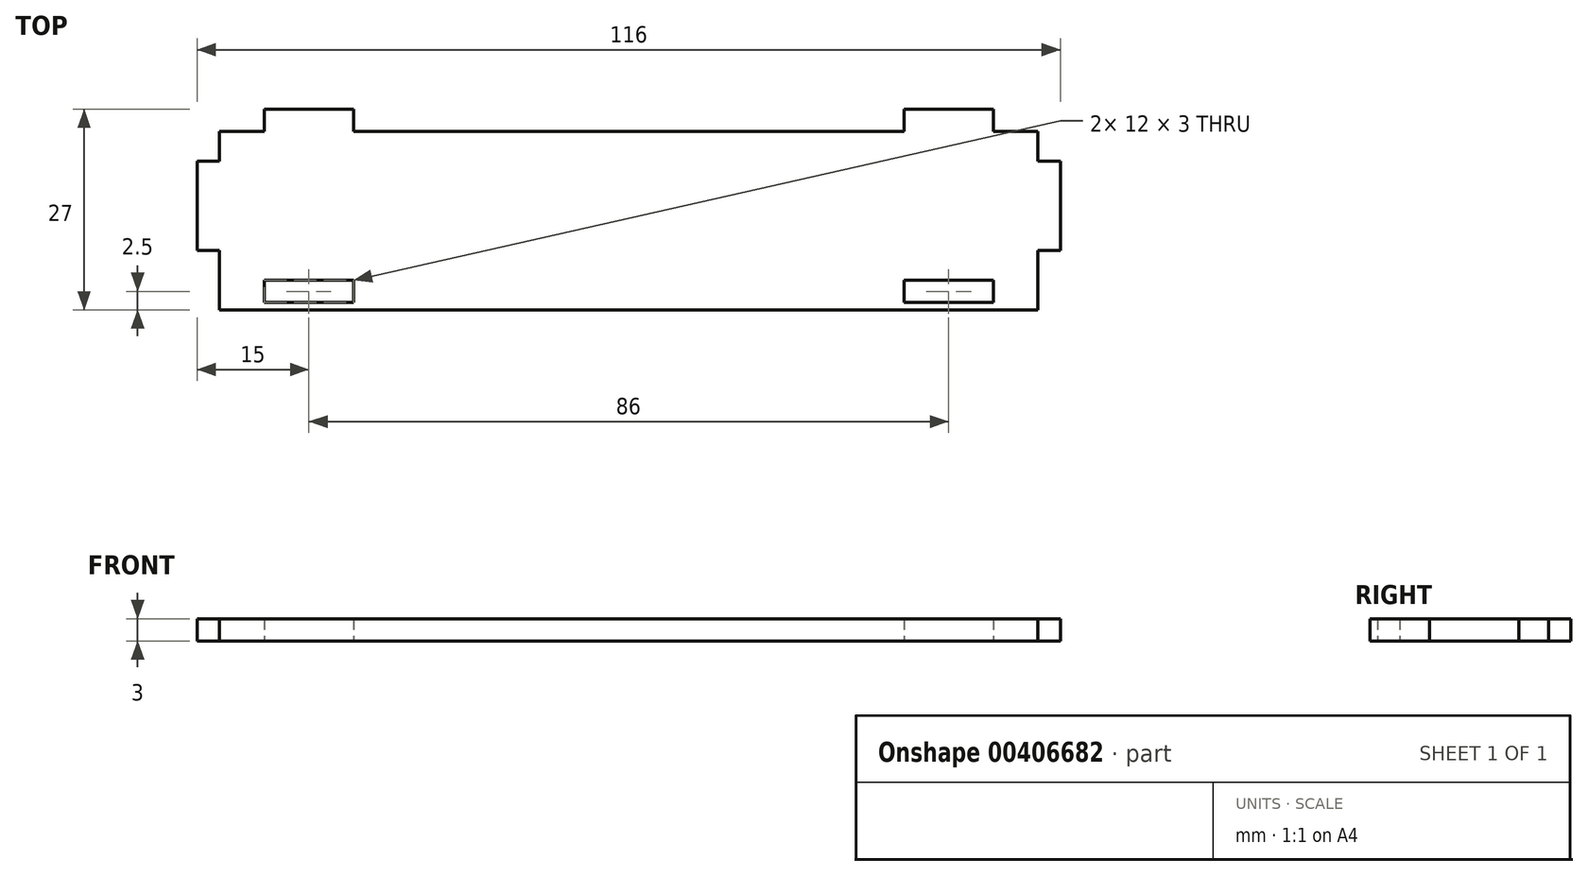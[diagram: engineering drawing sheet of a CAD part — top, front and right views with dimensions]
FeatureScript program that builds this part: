
annotation { "Feature Type Name" : "Feature", "Feature Type Description" : "" }
export const myFeature = defineFeature(function(context is Context, id is Id, definition is map)
    precondition{}
    {
        {
            var Q0;
            Q0=qCreatedBy(makeId("Top.planeOp"),FACE);
            var sketch = newSketch(context, id + "F0", { "sketchPlane" : qUnion([Q0])});
            skLineSegment(sketch, "E0.bottom", {"start": v(55, 12) * mm, "end": v(49, 12) * mm});
            skLineSegment(sketch, "E0.top", {"start": v(55, -12) * mm, "end": v(-55, -12) * mm});
            skLineSegment(sketch, "E0.left", {"start": v(55, 12) * mm, "end": v(55, 8) * mm});
            skLineSegment(sketch, "E0.right", {"start": v(-55, 12) * mm, "end": v(-55, 8) * mm});
            skPoint(sketch, "E0.middle", {"position": v(0, 0) * mm});
            skLineSegment(sketch, "E1.top", {"start": v(-49, 15) * mm, "end": v(-37, 15) * mm});
            skLineSegment(sketch, "E1.left", {"start": v(-49, 12) * mm, "end": v(-49, 15) * mm});
            skLineSegment(sketch, "E1.right", {"start": v(-37, 12) * mm, "end": v(-37, 15) * mm});
            skLineSegment(sketch, "E2.bottom", {"start": v(-49, -8) * mm, "end": v(-37, -8) * mm});
            skLineSegment(sketch, "E2.top", {"start": v(-49, -11) * mm, "end": v(-37, -11) * mm});
            skLineSegment(sketch, "E2.left", {"start": v(-49, -8) * mm, "end": v(-49, -11) * mm});
            skLineSegment(sketch, "E2.right", {"start": v(-37, -8) * mm, "end": v(-37, -11) * mm});
            skLineSegment(sketch, "E3.bottom", {"start": v(-55, 8) * mm, "end": v(-58, 8) * mm});
            skLineSegment(sketch, "E3.top", {"start": v(-55, -4) * mm, "end": v(-58, -4) * mm});
            skLineSegment(sketch, "E3.right", {"start": v(-58, 8) * mm, "end": v(-58, -4) * mm});
            skLineSegment(sketch, "E4", {"start": v(0, 0) * mm, "end": v(0, 12) * mm, "construction": true});
            skLineSegment(sketch, "E5.MirrorCS", {"start": v(37, 12) * mm, "end": v(37, 15) * mm});
            skLineSegment(sketch, "E6.MirrorCS", {"start": v(49, 15) * mm, "end": v(37, 15) * mm});
            skLineSegment(sketch, "E7.MirrorCS", {"start": v(49, 12) * mm, "end": v(49, 15) * mm});
            skLineSegment(sketch, "E8.MirrorCS", {"start": v(55, 8) * mm, "end": v(58, 8) * mm});
            skLineSegment(sketch, "E9.MirrorCS", {"start": v(58, 8) * mm, "end": v(58, -4) * mm});
            skLineSegment(sketch, "E10.MirrorCS", {"start": v(55, -4) * mm, "end": v(58, -4) * mm});
            skLineSegment(sketch, "E11.MirrorCS", {"start": v(49, -8) * mm, "end": v(37, -8) * mm});
            skLineSegment(sketch, "E12.MirrorCS", {"start": v(49, -8) * mm, "end": v(49, -11) * mm});
            skLineSegment(sketch, "E13.MirrorCS", {"start": v(49, -11) * mm, "end": v(37, -11) * mm});
            skLineSegment(sketch, "E14.MirrorCS", {"start": v(37, -8) * mm, "end": v(37, -11) * mm});
            skLineSegment(sketch, "E15.trimOffspring", {"start": v(-55, -4) * mm, "end": v(-55, -12) * mm});
            skLineSegment(sketch, "E16.trimOffspring", {"start": v(-49, 12) * mm, "end": v(-55, 12) * mm});
            skLineSegment(sketch, "E17.trimOffspring", {"start": v(37, 12) * mm, "end": v(-37, 12) * mm});
            skLineSegment(sketch, "E18.trimOffspring", {"start": v(55, -4) * mm, "end": v(55, -12) * mm});
            skSolve(sketch);
        }
        {
            var Q0;
            Q0=makeQuery(id+"F0.imprint","IMPRINT",FACE,{"disambiguationData":[TD([[makeQuery(id+"F0.imprint","IMPRINT",EDGE,{"derivedFrom":sQuery(id+"F0.wireOp",EDGE,"E0.bottom")}),1.0]])]});
            extrude(context, id + "F1", {"entities" : qUnion([Q0]), "depth" : 3 * mm});
        }
    });
